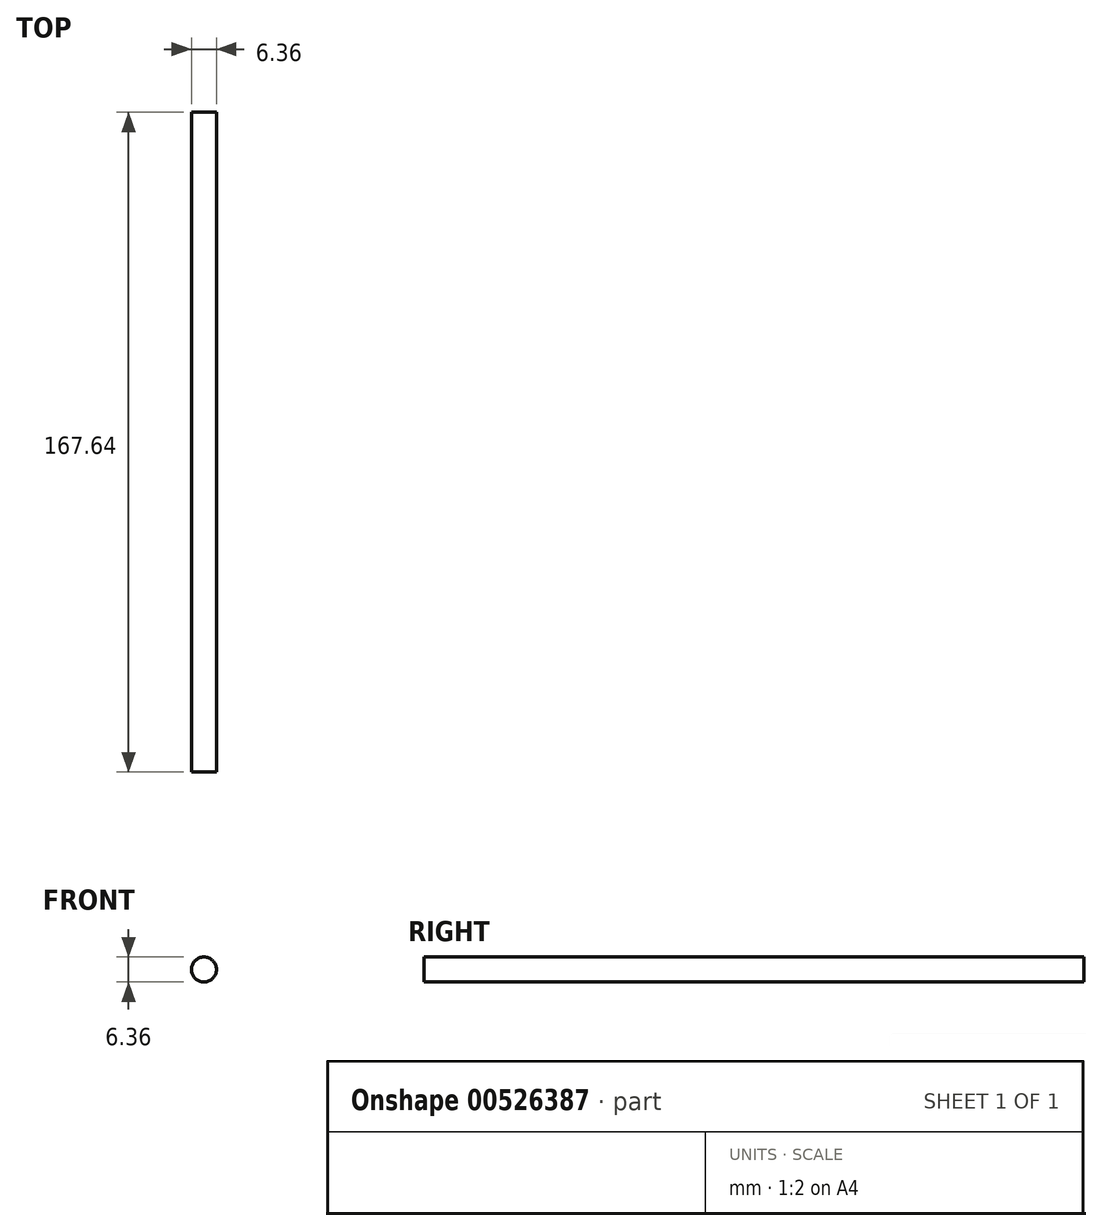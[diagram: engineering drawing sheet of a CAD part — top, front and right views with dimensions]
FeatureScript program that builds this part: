
annotation { "Feature Type Name" : "Feature", "Feature Type Description" : "" }
export const myFeature = defineFeature(function(context is Context, id is Id, definition is map)
    precondition{}
    {
        {
            var Q0;
            Q0=qCreatedBy(makeId("Front.planeOp"),FACE);
            var sketch = newSketch(context, id + "F0", { "sketchPlane" : qUnion([Q0])});
            skCircle(sketch, "E0", {"center": v(0, 0) * mm, "radius": 3.18 * mm});
            skSolve(sketch);
        }
        {
            var Q0;
            Q0 = qSketchRegion(id + "F0", true);
            extrude(context, id + "F1", {"entities" : qUnion([Q0]), "depth" : 167.64 * mm, "offsetDistance" : 25.4 * mm});
        }
    });
